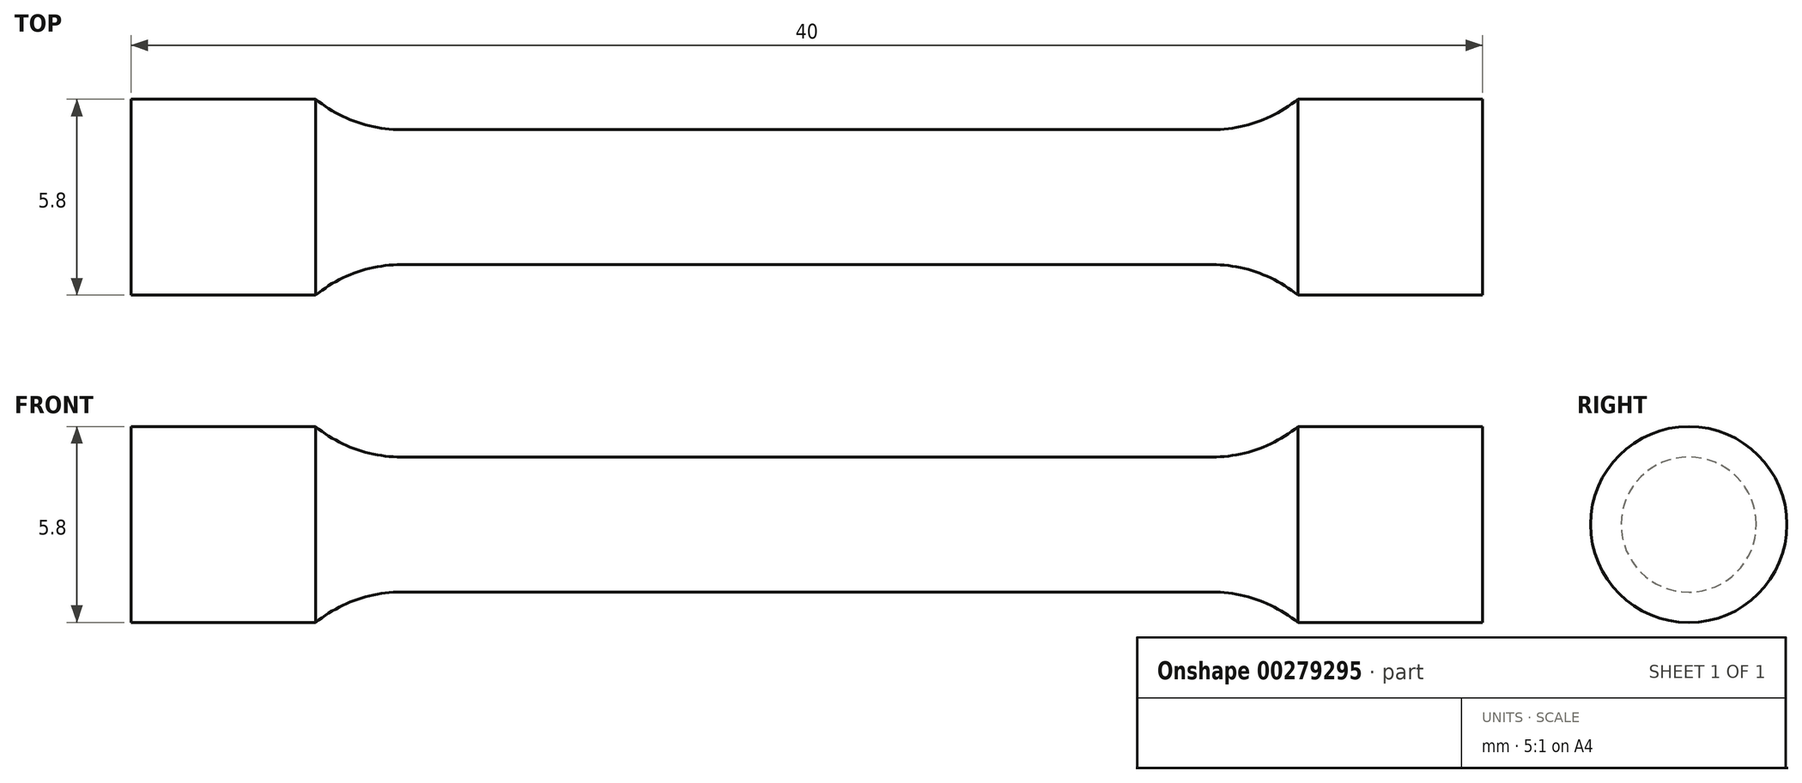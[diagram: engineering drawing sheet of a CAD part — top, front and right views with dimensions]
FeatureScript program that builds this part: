
annotation { "Feature Type Name" : "Feature", "Feature Type Description" : "" }
export const myFeature = defineFeature(function(context is Context, id is Id, definition is map)
    precondition{}
    {
        {
            var Q0;
            Q0=qCreatedBy(makeId("Front.planeOp"),FACE);
            var sketch = newSketch(context, id + "F0", { "sketchPlane" : qUnion([Q0])});
            skLineSegment(sketch, "E0", {"start": v(0, 2) * mm, "end": v(12, 2) * mm});
            skArc(sketch, "E1", {"start": v(12, 2) * mm, "mid": v(13.35, 2.23) * mm, "end": v(14.53, 2.9) * mm});
            skLineSegment(sketch, "E2", {"start": v(14.53, 2.9) * mm, "end": v(20, 2.9) * mm});
            skLineSegment(sketch, "E3", {"start": v(20, 2.9) * mm, "end": v(20, 0) * mm});
            skLineSegment(sketch, "E4", {"start": v(20, 0) * mm, "end": v(0, 0) * mm});
            skLineSegment(sketch, "E5.MirrorCS", {"start": v(0, 2) * mm, "end": v(-12, 2) * mm});
            skLineSegment(sketch, "E6.MirrorCS", {"start": v(-20, 0) * mm, "end": v(0, 0) * mm});
            skLineSegment(sketch, "E7.MirrorCS", {"start": v(-14.53, 2.9) * mm, "end": v(-20, 2.9) * mm});
            skLineSegment(sketch, "E8.MirrorCS", {"start": v(-20, 2.9) * mm, "end": v(-20, 0) * mm});
            skArc(sketch, "E9.MirrorCS", {"start": v(-12, 2) * mm, "mid": v(-13.35, 2.23) * mm, "end": v(-14.53, 2.9) * mm});
            skSolve(sketch);
        }
        {
            var Q0;
            Q0=makeQuery(id+"F0.imprint","IMPRINT",FACE,{"disambiguationData":[TD([[makeQuery(id+"F0.imprint","IMPRINT",EDGE,{"derivedFrom":sQuery(id+"F0.wireOp",EDGE,"E0")}),-1.0]])]});
            var Q1;
            Q1=sQuery(id+"F0.wireOp",EDGE,"E4");
            revolve(context, id + "F1", {"entities" : qUnion([Q0]), "axis" : qUnion([Q1]), "revolveType" : RevolveType.FULL});
        }
    });
